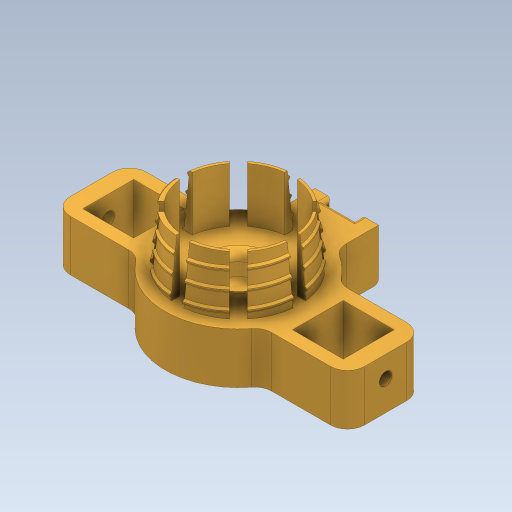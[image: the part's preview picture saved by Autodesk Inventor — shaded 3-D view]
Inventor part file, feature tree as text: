
AUTODESK INVENTOR PART (.ipt)
format: ipt  version: 2023 (Build 270158000, 158)  size: 2,116,096 bytes
history: native  units: mm
features: sketch x8, extrude x5, hole x3, fillet x3, helix x2, direct_edit x2, draft x1, mirror x1, other x1, revolve x1
ambient origin geometry x8: Origin, YZ Plane, XZ Plane, XY Plane, X Axis, Y Axis, Z Axis, Center Point
bodies: Solid1 (feature_tree)
feature tree (27):
  extrude  "Extrusion1"  Depth=12.875mm
  draft  "FaceDraft1"
  sketch  "Sketch2"  dims[d34=0.0mm d35=0.0mm d56=8.726646mm]
  helix  "Coil3"  [1 undecoded]
  helix  "Coil4"  [1 undecoded]
  direct_edit  "Direct Edit2"
  extrude  "Extrusion2"  Depth=8.726646mm
  extrude  "Extrusion13"  TaperAngle=90.0deg  [1 undecoded]
  extrude  "Extrusion14"  Depth=34.58632mm
  hole  "Hole3"  [1 undecoded]
  hole  "Hole4"  [1 undecoded]
  fillet  "Fillet11"  Radius=3.0mm
  fillet  "Fillet12"  Radius=80.0mm
  hole  "Hole5"  [1 undecoded]
  mirror  "Mirror2"
  extrude  "Extrusion15"  Depth=1.0mm
  direct_edit  "Direct Edit3"
  fillet  "Fillet13"  Radius=18.0mm
  sketch  "Sketch1"  dims[d0=25.0mm d1=26.5mm d2=12.875mm d3=0.0mm d4=1.047198mm]
  sketch  "Sketch3"  dims[d62=4.0mm d63=13.0mm d64=10.0mm d65=1.047198mm]
  sketch  "Sketch11"  dims[d66=90.0deg d67=90.0deg d68=0.0mm d69=0.0mm d70=4.0mm d71=3.0mm d72=10.0mm d73=-1.047198mm d74=90.0deg d75=90.0deg d76=0.0mm d77=0.0mm]
  sketch  "Sketch13"  dims[d79=-0.127mm d145=34.58632mm]
  sketch  "Sketch14"  dims[d150=120.0deg d151=120.0deg]
  sketch  "Sketch15"  dims[d153=21.6866mm d157=12.0mm d158=0.0mm d159=3.0mm d160=80.0mm d162=360.0deg]
  sketch  "Sketch16"  dims[d164=0.0mm d165=0.0mm d179=5.3mm d180=6.0mm d181=4.0mm d182=2.0mm d183=90.0deg d184=5.0mm d185=0.0mm d186=10.0mm d187=6.0mm d188=4.0mm d189=2.0mm d190=90.0deg d191=7.0mm d192=0.0mm d193=2.0mm d194=20.0mm d195=18.0mm d196=12.0mm d197=10.0mm d198=4.0mm d199=3.0mm d200=6.0mm d201=3.01mm d202=2.0mm d203=14.3117mm d204=8.0mm d205=0.0mm d206=15.0mm d207=10.0mm d208=7.0mm d209=10.0mm d210=1.0mm d211=0.0mm d212=-4.363323mm d213=1.0mm d109=0.5mm d110=0.872665mm d111=0.5mm d112=0.872665mm]
  other  "Size2"
  revolve  "Rotate1"  [1 undecoded]
note: 7 required parameter values undecoded (feature->parameter linkage not recoverable at this tier; creation-order binding heuristic only, values carry confidence <= 0.55)